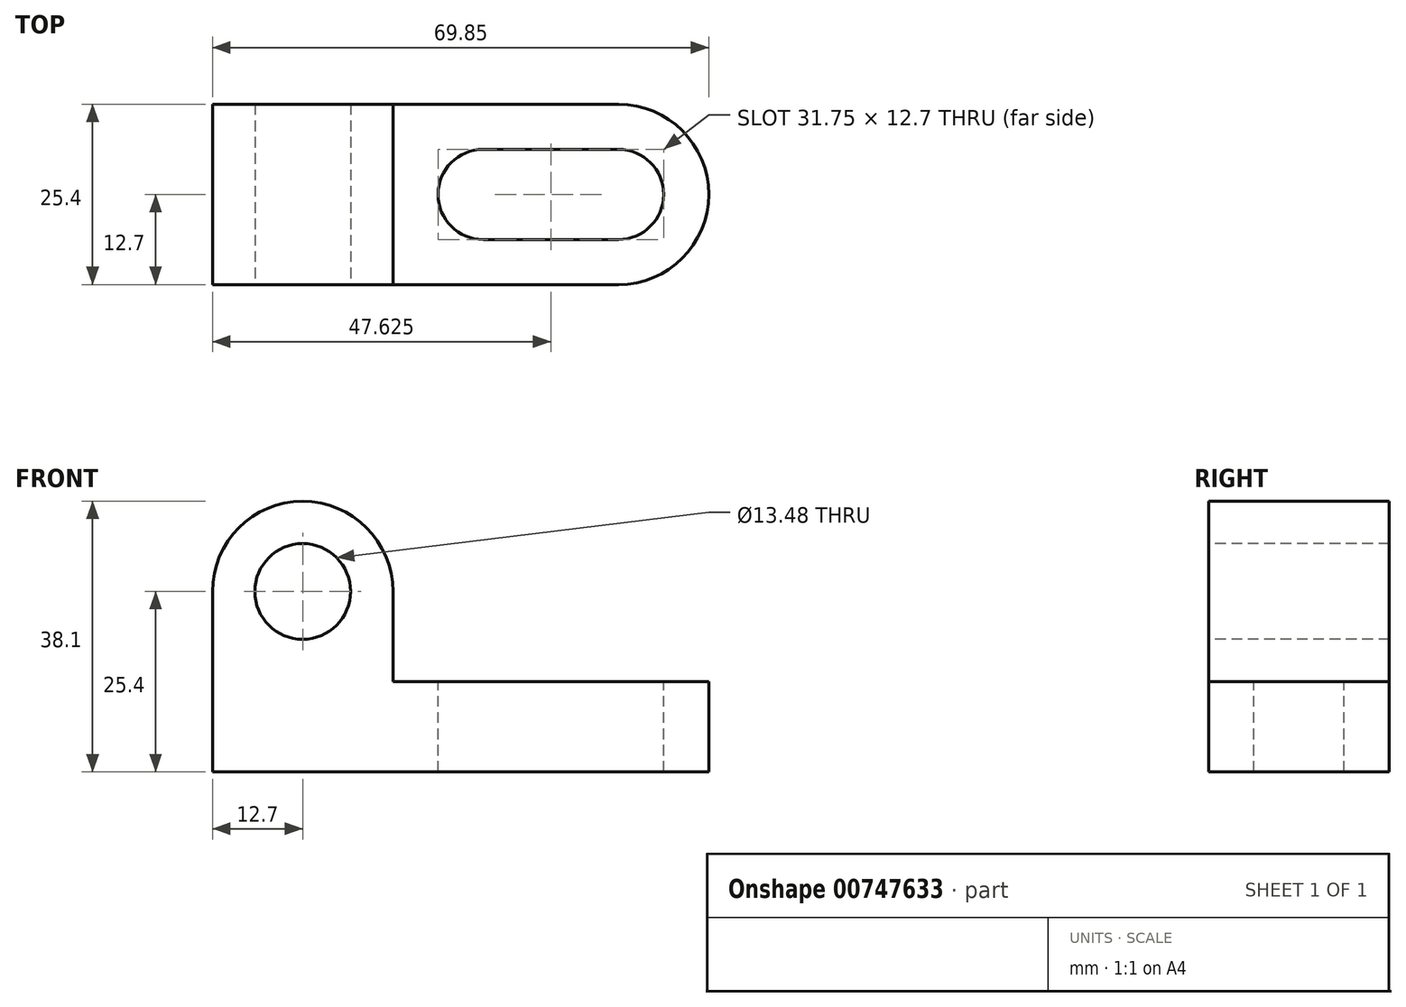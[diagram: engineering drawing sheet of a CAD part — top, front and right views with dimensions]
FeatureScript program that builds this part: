
annotation { "Feature Type Name" : "Feature", "Feature Type Description" : "" }
export const myFeature = defineFeature(function(context is Context, id is Id, definition is map)
    precondition{}
    {
        {
            var Q0;
            Q0=qCreatedBy(makeId("Front.planeOp"),FACE);
            var sketch = newSketch(context, id + "F0", { "sketchPlane" : qUnion([Q0])});
            skLineSegment(sketch, "E0", {"start": v(0, 0) * mm, "end": v(69.85, 0) * mm});
            skLineSegment(sketch, "E1", {"start": v(69.85, 0) * mm, "end": v(69.85, 38.1) * mm});
            skLineSegment(sketch, "E2", {"start": v(69.85, 38.1) * mm, "end": v(0, 38.1) * mm});
            skLineSegment(sketch, "E3", {"start": v(0, 38.1) * mm, "end": v(0, 0) * mm});
            skSolve(sketch);
        }
        {
            var Q0;
            Q0 = qSketchRegion(id + "F0", true);
            extrude(context, id + "F1", {"entities" : qUnion([Q0]), "oppositeDirection" : true, "depth" : 25.4 * mm, "offsetDistance" : 25.4 * mm});
        }
        {
            var Q0;
            Q0=makeQuery(id+"F1.opExtrude","CAP_FACE",FACE,{"disambiguationData":[OSD([sQuery(id+"F0.wireOp",EDGE,"E0"),sQuery(id+"F0.wireOp",EDGE,"E1"),sQuery(id+"F0.wireOp",EDGE,"E2"),sQuery(id+"F0.wireOp",EDGE,"E3")])],"isStart":true});
            var sketch = newSketch(context, id + "F2", { "sketchPlane" : qUnion([Q0])});
            skLineSegment(sketch, "E4", {"start": v(25.4, 38.1) * mm, "end": v(25.4, 12.7) * mm});
            skLineSegment(sketch, "E5", {"start": v(25.4, 12.7) * mm, "end": v(69.85, 12.7) * mm});
            skSolve(sketch);
        }
        {
            var Q0;
            Q0 = qSketchRegion(id + "F2", true);
            var Q1;
            {var subQ0=sQuery(id+"F2.wireOp",EDGE,"E4");Q1=makeQuery(id+"F2.imprint","IMPRINT",FACE,{"disambiguationData":[TD([[makeQuery(id+"F2.imprint","IMPRINT",EDGE,{"derivedFrom":subQ0}),1.0]])]});}
            extrude(context, id + "F3", {"entities" : qUnion([Q0, Q1]), "operationType" : NewBodyOperationType.REMOVE, "oppositeDirection" : true, "depth" : 25.4 * mm, "offsetDistance" : 25.4 * mm});
        }
        {
            var Q0;
            Q0=makeQuery(id+"F3.boolean.opBoolean","COPY",FACE,{"derivedFrom":makeQuery(id+"F3.opExtrude","SWEPT_FACE",FACE,{"disambiguationData":[OSD([sQuery(id+"F2.wireOp",EDGE,"E5")])]})});
            var sketch = newSketch(context, id + "F4", { "sketchPlane" : qUnion([Q0])});
            skCircle(sketch, "E6", {"center": v(38.1, 12.7) * mm, "radius": 6.35 * mm});
            skCircle(sketch, "E7", {"center": v(57.15, 12.7) * mm, "radius": 6.35 * mm});
            skLineSegment(sketch, "E8", {"start": v(38.1, 6.35) * mm, "end": v(57.15, 6.35) * mm});
            skLineSegment(sketch, "E9", {"start": v(38.1, 19.05) * mm, "end": v(57.15, 19.05) * mm});
            skSolve(sketch);
        }
        {
            var Q0;
            {var subQ0=sQuery(id+"F4.wireOp",EDGE,"E6");var subQ1=makeQuery(id+"F4.imprint","INTERSECT",VERTEX,{"derivedFrom":[subQ0,sQuery(id+"F4.wireOp",EDGE,"E8")]});Q0=makeQuery(id+"F4.imprint","IMPRINT",FACE,{"disambiguationData":[TD([[makeQuery(id+"F4.imprint","IMPRINT",EDGE,{"disambiguationData":[TD([[subQ1,1.0]])],"derivedFrom":subQ0}),1.0]])]});}
            var Q1;
            {var subQ0=sQuery(id+"F4.wireOp",EDGE,"E8");Q1=makeQuery(id+"F4.imprint","IMPRINT",FACE,{"disambiguationData":[TD([[makeQuery(id+"F4.imprint","IMPRINT",EDGE,{"derivedFrom":subQ0}),1.0]])]});}
            var Q2;
            {var subQ0=sQuery(id+"F4.wireOp",EDGE,"E7");var subQ1=makeQuery(id+"F4.imprint","INTERSECT",VERTEX,{"derivedFrom":[subQ0,sQuery(id+"F4.wireOp",EDGE,"E8")]});Q2=makeQuery(id+"F4.imprint","IMPRINT",FACE,{"disambiguationData":[TD([[makeQuery(id+"F4.imprint","IMPRINT",EDGE,{"disambiguationData":[TD([[subQ1,1.0]])],"derivedFrom":subQ0}),1.0]])]});}
            extrude(context, id + "F5", {"entities" : qUnion([Q0, Q1, Q2]), "operationType" : NewBodyOperationType.REMOVE, "oppositeDirection" : true, "depth" : 25.4 * mm, "offsetDistance" : 25.4 * mm});
        }
        {
            var Q0;
            Q0=makeQuery(id+"F3.boolean.opBoolean","COPY",FACE,{"derivedFrom":makeQuery(id+"F3.opExtrude","SWEPT_FACE",FACE,{"disambiguationData":[OSD([sQuery(id+"F2.wireOp",EDGE,"E5")])]})});
            var sketch = newSketch(context, id + "F6", { "sketchPlane" : qUnion([Q0])});
            skArc(sketch, "E10", {"start": v(57.15, 0) * mm, "mid": v(69.85, 12.7) * mm, "end": v(57.15, 25.4) * mm});
            skSolve(sketch);
        }
        {
            var Q0;
            Q0 = qSketchRegion(id + "F6", true);
            var Q1;
            {var subQ0=sQuery(id+"F6.wireOp",EDGE,"E10");var subQ1=sQuery(id+"F2.wireOp",EDGE,"E5");var subQ2=makeQuery(id+"F3.boolean.opBoolean","COPY",EDGE,{"derivedFrom":makeQuery(id+"F3.opExtrude","CAP_EDGE",EDGE,{"disambiguationData":[OSD([subQ1])],"isStart":false})});var subQ3=makeQuery(id+"F6.imprint","INTERSECT",VERTEX,{"derivedFrom":[subQ2,subQ0]});Q1=makeQuery(id+"F6.imprint","IMPRINT",FACE,{"disambiguationData":[TD([[makeQuery(id+"F6.imprint","IMPRINT",EDGE,{"disambiguationData":[TD([[subQ3,1.0]])],"derivedFrom":subQ0}),-1.0]])]});}
            var Q2;
            {var subQ0=sQuery(id+"F6.wireOp",EDGE,"E10");var subQ1=sQuery(id+"F2.wireOp",EDGE,"E5");var subQ2=makeQuery(id+"F3.boolean.opBoolean","COPY",EDGE,{"derivedFrom":makeQuery(id+"F3.opExtrude","CAP_EDGE",EDGE,{"disambiguationData":[OSD([subQ1])],"isStart":true})});var subQ3=makeQuery(id+"F6.imprint","INTERSECT",VERTEX,{"derivedFrom":[subQ2,subQ0]});Q2=makeQuery(id+"F6.imprint","IMPRINT",FACE,{"disambiguationData":[TD([[makeQuery(id+"F6.imprint","IMPRINT",EDGE,{"disambiguationData":[TD([[subQ3,-1.0]])],"derivedFrom":subQ0}),-1.0]])]});}
            extrude(context, id + "F7", {"entities" : qUnion([Q0, Q1, Q2]), "operationType" : NewBodyOperationType.REMOVE, "oppositeDirection" : true, "depth" : 25.4 * mm, "offsetDistance" : 25.4 * mm});
        }
        {
            var Q0;
            Q0=makeQuery(id+"F1.opExtrude","CAP_FACE",FACE,{"disambiguationData":[OSD([sQuery(id+"F0.wireOp",EDGE,"E0"),sQuery(id+"F0.wireOp",EDGE,"E1"),sQuery(id+"F0.wireOp",EDGE,"E2"),sQuery(id+"F0.wireOp",EDGE,"E3")])],"isStart":true});
            var sketch = newSketch(context, id + "F8", { "sketchPlane" : qUnion([Q0])});
            skCircle(sketch, "E11", {"center": v(12.7, 25.4) * mm, "radius": 6.74 * mm});
            skSolve(sketch);
        }
        {
            var Q0;
            Q0=makeQuery(id+"F8.imprint","IMPRINT",FACE,{"disambiguationData":[TD([[makeQuery(id+"F8.imprint","IMPRINT",EDGE,{"derivedFrom":sQuery(id+"F8.wireOp",EDGE,"E11")}),1.0]])]});
            extrude(context, id + "F9", {"entities" : qUnion([Q0]), "operationType" : NewBodyOperationType.REMOVE, "oppositeDirection" : true, "depth" : 25.4 * mm, "offsetDistance" : 25.4 * mm});
        }
        {
            var Q0;
            Q0=makeQuery(id+"F1.opExtrude","CAP_FACE",FACE,{"disambiguationData":[OSD([sQuery(id+"F0.wireOp",EDGE,"E0"),sQuery(id+"F0.wireOp",EDGE,"E1"),sQuery(id+"F0.wireOp",EDGE,"E2"),sQuery(id+"F0.wireOp",EDGE,"E3")])],"isStart":true});
            var sketch = newSketch(context, id + "F10", { "sketchPlane" : qUnion([Q0])});
            skArc(sketch, "E12", {"start": v(25.4, 25.4) * mm, "mid": v(12.7, 38.1) * mm, "end": v(0, 25.4) * mm});
            skSolve(sketch);
        }
        {
            var Q0;
            {var subQ0=sQuery(id+"F10.wireOp",EDGE,"E12");var subQ1=makeQuery(id+"F1.opExtrude","CAP_EDGE",EDGE,{"disambiguationData":[OSD([sQuery(id+"F0.wireOp",EDGE,"E3")])],"isStart":true});var subQ2=makeQuery(id+"F10.imprint","INTERSECT",VERTEX,{"derivedFrom":[subQ1,subQ0]});Q0=makeQuery(id+"F10.imprint","IMPRINT",FACE,{"disambiguationData":[TD([[makeQuery(id+"F10.imprint","IMPRINT",EDGE,{"disambiguationData":[TD([[subQ2,1.0]])],"derivedFrom":subQ0}),-1.0]])]});}
            var Q1;
            {var subQ0=sQuery(id+"F10.wireOp",EDGE,"E12");var subQ1=makeQuery(id+"F3.boolean.opBoolean","COPY",EDGE,{"derivedFrom":makeQuery(id+"F3.opExtrude","CAP_EDGE",EDGE,{"disambiguationData":[OSD([sQuery(id+"F2.wireOp",EDGE,"E4")])],"isStart":true})});var subQ2=makeQuery(id+"F10.imprint","INTERSECT",VERTEX,{"derivedFrom":[subQ1,subQ0]});Q1=makeQuery(id+"F10.imprint","IMPRINT",FACE,{"disambiguationData":[TD([[makeQuery(id+"F10.imprint","IMPRINT",EDGE,{"disambiguationData":[TD([[subQ2,-1.0]])],"derivedFrom":subQ0}),-1.0]])]});}
            extrude(context, id + "F11", {"entities" : qUnion([Q0, Q1]), "operationType" : NewBodyOperationType.REMOVE, "oppositeDirection" : true, "depth" : 25.4 * mm, "offsetDistance" : 25.4 * mm});
        }
    });
